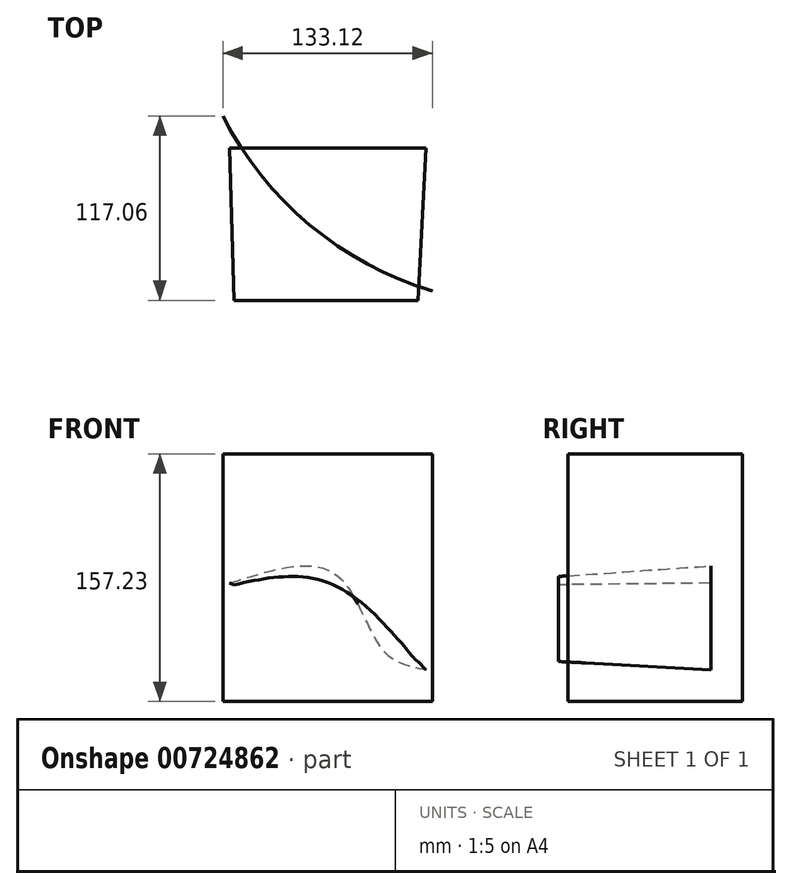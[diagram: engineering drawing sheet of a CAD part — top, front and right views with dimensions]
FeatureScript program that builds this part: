
annotation { "Feature Type Name" : "Feature", "Feature Type Description" : "" }
export const myFeature = defineFeature(function(context is Context, id is Id, definition is map)
    precondition{}
    {
        {
            var Q0;
            Q0=qCreatedBy(makeId("Front.planeOp"),FACE);
            var sketch = newSketch(context, id + "F0", { "sketchPlane" : qUnion([Q0])});
            skFitSpline(sketch, "E0", {"points": [v(-58.13, 49.72) * mm, v(8.53, 55.7) * mm, v(38.86, 7.58) * mm, v(66.66, -5.24) * mm], "startDerivative": vector(199.43, 64.72) * mm, "endDerivative": vector(116.42, -21.4) * mm});
            skSolve(sketch);
        }
        {
            var Q0;
            Q0=qCreatedBy(makeId("Front.planeOp"),FACE);
            cPlane(context, id + "F1", {"entities" : qUnion([Q0]), "cplaneType" : CPlaneType.OFFSET, "offset" : 96.77 * mm, "width" : 152.4 * mm, "height" : 152.4 * mm});
        }
        {
            var Q0;
            Q0=qCreatedBy(id+"F1.planeOp",FACE);
            var sketch = newSketch(context, id + "F2", { "sketchPlane" : qUnion([Q0])});
            skFitSpline(sketch, "E1", {"points": [v(-55.35, 48.68) * mm, v(14.53, 45.18) * mm, v(61.11, 0) * mm, v(61.49, 0) * mm], "startDerivative": vector(143.13, 31.06) * mm, "endDerivative": vector(7.36, 4.68) * mm});
            skSolve(sketch);
        }
        {
            var Q0;
            Q0 = qSketchRegion(id + "F0", true);
            var Q1;
            Q1 = qSketchRegion(id + "F2", true);
            var Q2;
            Q2=sQuery(id+"F0.wireOp",EDGE,"E0");
            var Q3;
            Q3=sQuery(id+"F2.wireOp",EDGE,"E1");
            loft(context, id + "F3", {"bodyType" : ToolBodyType.SURFACE, "sheetProfilesArray" : [{ "sheetProfileEntities" : qUnion([Q0]) }, { "sheetProfileEntities" : qUnion([Q1]) }], "wireProfilesArray" : [{ "wireProfileEntities" : qUnion([Q2]) }, { "wireProfileEntities" : qUnion([Q3]) }]});
        }
        {
            var Q0;
            Q0=qCreatedBy(makeId("Top.planeOp"),FACE);
            var sketch = newSketch(context, id + "F4", { "sketchPlane" : qUnion([Q0])});
            skArc(sketch, "E2", {"start": v(-62.5, 20.3) * mm, "mid": v(-7.3, -48.84) * mm, "end": v(70.6, -90.74) * mm});
            skSolve(sketch);
        }
        {
            var Q0;
            Q0 = qSketchRegion(id + "F4", true);
            var Q1;
            Q1=sQuery(id+"F4.wireOp",EDGE,"E2");
            extrude(context, id + "F5", {"entities" : qUnion([Q0]), "bodyType" : ToolBodyType.SURFACE, "surfaceEntities" : qUnion([Q1]), "depth" : 131.83 * mm, "offsetDistance" : 25.4 * mm, "hasSecondDirection" : true, "secondDirectionOppositeDirection" : true, "secondDirectionDepth" : 25.4 * mm});
        }
    });
